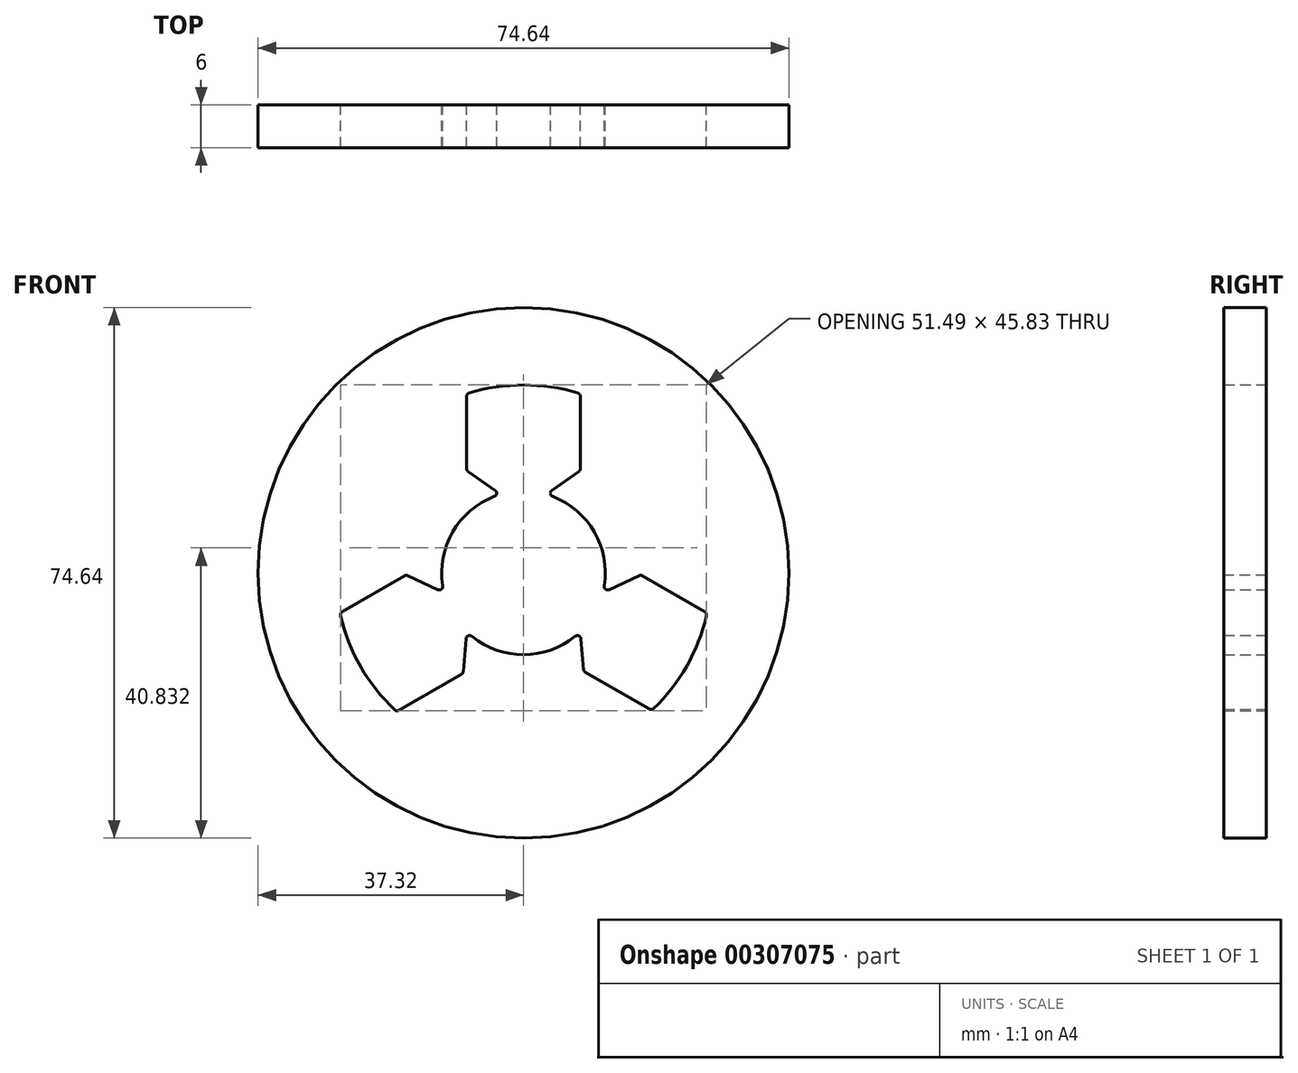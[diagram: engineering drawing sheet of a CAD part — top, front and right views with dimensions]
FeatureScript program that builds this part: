
annotation { "Feature Type Name" : "Feature", "Feature Type Description" : "" }
export const myFeature = defineFeature(function(context is Context, id is Id, definition is map)
    precondition{}
    {
        {
            var Q0;
            Q0=qCreatedBy(makeId("Front.planeOp"),FACE);
            var sketch = newSketch(context, id + "F0", { "sketchPlane" : qUnion([Q0])});
            skArc(sketch, "E0", {"start": v(-3.18, 11.05) * mm, "mid": v(-10, 5.7) * mm, "end": v(-11.13, -2.9) * mm});
            skLineSegment(sketch, "E1", {"start": v(0, 0) * mm, "end": v(0, 30.05) * mm, "construction": true});
            skLineSegment(sketch, "E2", {"start": v(0, 0) * mm, "end": v(-23.38, -13.5) * mm, "construction": true});
            skLineSegment(sketch, "E3", {"start": v(0, 0) * mm, "end": v(23.75, -13.71) * mm, "construction": true});
            skLineSegment(sketch, "E4", {"start": v(-1.5, 10) * mm, "end": v(1.5, 10) * mm, "construction": true});
            skLineSegment(sketch, "E5", {"start": v(1.5, 10) * mm, "end": v(7.5, 14.2) * mm, "construction": true});
            skLineSegment(sketch, "E6", {"start": v(7.5, 14.2) * mm, "end": v(7.5, 23.6) * mm, "construction": true});
            skLineSegment(sketch, "E7", {"start": v(-7.5, 23.6) * mm, "end": v(-7.5, 14.2) * mm, "construction": true});
            skLineSegment(sketch, "E8", {"start": v(-7.5, 14.2) * mm, "end": v(-1.5, 10) * mm, "construction": true});
            skArc(sketch, "E9", {"start": v(7.5, 23.6) * mm, "mid": v(0, 26) * mm, "end": v(-7.5, 23.6) * mm, "construction": true});
            skLineSegment(sketch, "E10", {"start": v(-8, 25.19) * mm, "end": v(-8, 14.43) * mm});
            skLineSegment(sketch, "E11", {"start": v(-8, 14.43) * mm, "end": v(-3.18, 11.05) * mm});
            skLineSegment(sketch, "E12", {"start": v(8, 25.19) * mm, "end": v(8, 14.43) * mm});
            skLineSegment(sketch, "E13", {"start": v(8, 14.43) * mm, "end": v(3.18, 11.05) * mm});
            skLineSegment(sketch, "E14", {"start": v(9.41, -3.7) * mm, "end": v(7.91, -6.3) * mm, "construction": true});
            skLineSegment(sketch, "E15", {"start": v(7.91, -6.3) * mm, "end": v(8.55, -13.6) * mm, "construction": true});
            skLineSegment(sketch, "E16", {"start": v(8.55, -13.6) * mm, "end": v(16.7, -18.3) * mm, "construction": true});
            skLineSegment(sketch, "E17", {"start": v(24.2, -5.3) * mm, "end": v(16.05, -0.6) * mm, "construction": true});
            skLineSegment(sketch, "E18", {"start": v(16.05, -0.6) * mm, "end": v(9.41, -3.7) * mm, "construction": true});
            skLineSegment(sketch, "E19", {"start": v(-9.41, -3.7) * mm, "end": v(-7.91, -6.3) * mm, "construction": true});
            skLineSegment(sketch, "E20", {"start": v(-7.91, -6.3) * mm, "end": v(-8.55, -13.6) * mm, "construction": true});
            skLineSegment(sketch, "E21", {"start": v(-8.55, -13.6) * mm, "end": v(-16.7, -18.3) * mm, "construction": true});
            skLineSegment(sketch, "E22", {"start": v(-24.2, -5.3) * mm, "end": v(-16.05, -0.6) * mm, "construction": true});
            skLineSegment(sketch, "E23", {"start": v(-16.05, -0.6) * mm, "end": v(-9.41, -3.7) * mm, "construction": true});
            skArc(sketch, "E24", {"start": v(16.7, -18.3) * mm, "mid": v(22.72, -13.12) * mm, "end": v(24.2, -5.3) * mm, "construction": true});
            skArc(sketch, "E25", {"start": v(-24.2, -5.3) * mm, "mid": v(-22.72, -13.12) * mm, "end": v(-16.7, -18.3) * mm, "construction": true});
            skLineSegment(sketch, "E26", {"start": v(-11.16, -2.77) * mm, "end": v(-16.5, -0.29) * mm});
            skLineSegment(sketch, "E27", {"start": v(-7.98, -8.28) * mm, "end": v(-8.5, -14.14) * mm});
            skLineSegment(sketch, "E28", {"start": v(7.98, -8.28) * mm, "end": v(8.47, -13.84) * mm});
            skLineSegment(sketch, "E29", {"start": v(11.16, -2.77) * mm, "end": v(16.5, -0.29) * mm});
            skLineSegment(sketch, "E30", {"start": v(16.5, -0.29) * mm, "end": v(25.81, -5.67) * mm});
            skLineSegment(sketch, "E31", {"start": v(8.47, -13.84) * mm, "end": v(18, -19.35) * mm});
            skLineSegment(sketch, "E32", {"start": v(-8.5, -14.14) * mm, "end": v(-17.81, -19.52) * mm});
            skLineSegment(sketch, "E33", {"start": v(-16.5, -0.29) * mm, "end": v(-25.81, -5.67) * mm});
            skArc(sketch, "E34.trimOffspring", {"start": v(11.13, -2.9) * mm, "mid": v(10, 5.7) * mm, "end": v(3.18, 11.05) * mm});
            skArc(sketch, "E35.trimOffspring", {"start": v(-8.08, -8.19) * mm, "mid": v(0, -11.5) * mm, "end": v(8.08, -8.19) * mm});
            skLineSegment(sketch, "E36", {"start": v(21.55, -15.3) * mm, "end": v(23.78, -11.54) * mm});
            skCircle(sketch, "E37", {"center": v(0, 0) * mm, "radius": 37.32 * mm});
            skArc(sketch, "E38", {"start": v(-25.81, -5.67) * mm, "mid": v(-22.89, -13.21) * mm, "end": v(-17.81, -19.52) * mm});
            skArc(sketch, "E39.trimOffspring", {"start": v(8, 25.19) * mm, "mid": v(0, 26.43) * mm, "end": v(-8, 25.19) * mm});
            skArc(sketch, "E40.trimOffspring", {"start": v(18, -19.35) * mm, "mid": v(22.95, -13.1) * mm, "end": v(25.81, -5.67) * mm});
            skSolve(sketch);
        }
        {
            var Q0;
            Q0 = qSketchRegion(id + "F0", true);
            extrude(context, id + "F1", {"entities" : qUnion([Q0]), "depth" : 6 * mm});
        }
        {
            var Q0;
            Q0=makeQuery(id+"F1.opExtrude","SWEPT_EDGE",EDGE,{"disambiguationData":[OSD([sQuery(id+"F0.wireOp",EDGE,"E12"),sQuery(id+"F0.wireOp",EDGE,"4N6ULIY0-qUOi-bycz-Wa86-CKs5s0DuueQi")])]});
            var Q1;
            Q1=makeQuery(id+"F1.opExtrude","SWEPT_EDGE",EDGE,{"disambiguationData":[OSD([sQuery(id+"F0.wireOp",EDGE,"E10"),sQuery(id+"F0.wireOp",EDGE,"4N6ULIY0-qUOi-bycz-Wa86-CKs5s0DuueQi")])]});
            var Q2;
            Q2=makeQuery(id+"F1.opExtrude","SWEPT_EDGE",EDGE,{"disambiguationData":[OSD([sQuery(id+"F0.wireOp",EDGE,"E33"),sQuery(id+"F0.wireOp",EDGE,"3BcPhAl4-HTEZ-S3qT-W1Qs-juj69pW5knXt")])]});
            var Q3;
            Q3=makeQuery(id+"F1.opExtrude","SWEPT_EDGE",EDGE,{"disambiguationData":[OSD([sQuery(id+"F0.wireOp",EDGE,"E32"),sQuery(id+"F0.wireOp",EDGE,"3BcPhAl4-HTEZ-S3qT-W1Qs-juj69pW5knXt")])]});
            var Q4;
            Q4=makeQuery(id+"F1.opExtrude","SWEPT_EDGE",EDGE,{"disambiguationData":[OSD([sQuery(id+"F0.wireOp",EDGE,"E31"),sQuery(id+"F0.wireOp",EDGE,"E36")])]});
            var Q5;
            Q5=makeQuery(id+"F1.opExtrude","SWEPT_EDGE",EDGE,{"disambiguationData":[OSD([sQuery(id+"F0.wireOp",EDGE,"E30"),sQuery(id+"F0.wireOp",EDGE,"E36")])]});
            fillet(context, id + "F2", {"entities" : qUnion([Q0, Q1, Q2, Q3, Q4, Q5]), "radius" : 0.5 * mm, "tangentPropagation" : true, "allowEdgeOverflow" : false});
        }
        {
            var Q0;
            Q0=makeQuery(id+"F1.opExtrude","SWEPT_EDGE",EDGE,{"disambiguationData":[OSD([sQuery(id+"F0.wireOp",EDGE,"E13"),sQuery(id+"F0.wireOp",EDGE,"E34.trimOffspring")])]});
            var Q1;
            Q1=makeQuery(id+"F1.opExtrude","SWEPT_EDGE",EDGE,{"disambiguationData":[OSD([sQuery(id+"F0.wireOp",EDGE,"E29"),sQuery(id+"F0.wireOp",EDGE,"E34.trimOffspring")])]});
            var Q2;
            Q2=makeQuery(id+"F1.opExtrude","SWEPT_EDGE",EDGE,{"disambiguationData":[OSD([sQuery(id+"F0.wireOp",EDGE,"E28"),sQuery(id+"F0.wireOp",EDGE,"E35.trimOffspring")])]});
            var Q3;
            Q3=makeQuery(id+"F1.opExtrude","SWEPT_EDGE",EDGE,{"disambiguationData":[OSD([sQuery(id+"F0.wireOp",EDGE,"E0"),sQuery(id+"F0.wireOp",EDGE,"E26")])]});
            var Q4;
            Q4=makeQuery(id+"F1.opExtrude","SWEPT_EDGE",EDGE,{"disambiguationData":[OSD([sQuery(id+"F0.wireOp",EDGE,"E27"),sQuery(id+"F0.wireOp",EDGE,"E35.trimOffspring")])]});
            var Q5;
            Q5=makeQuery(id+"F1.opExtrude","SWEPT_EDGE",EDGE,{"disambiguationData":[OSD([sQuery(id+"F0.wireOp",EDGE,"E0"),sQuery(id+"F0.wireOp",EDGE,"E11")])]});
            fillet(context, id + "F3", {"entities" : qUnion([Q0, Q1, Q2, Q3, Q4, Q5]), "radius" : 0.5 * mm, "tangentPropagation" : true, "allowEdgeOverflow" : false});
        }
    });
